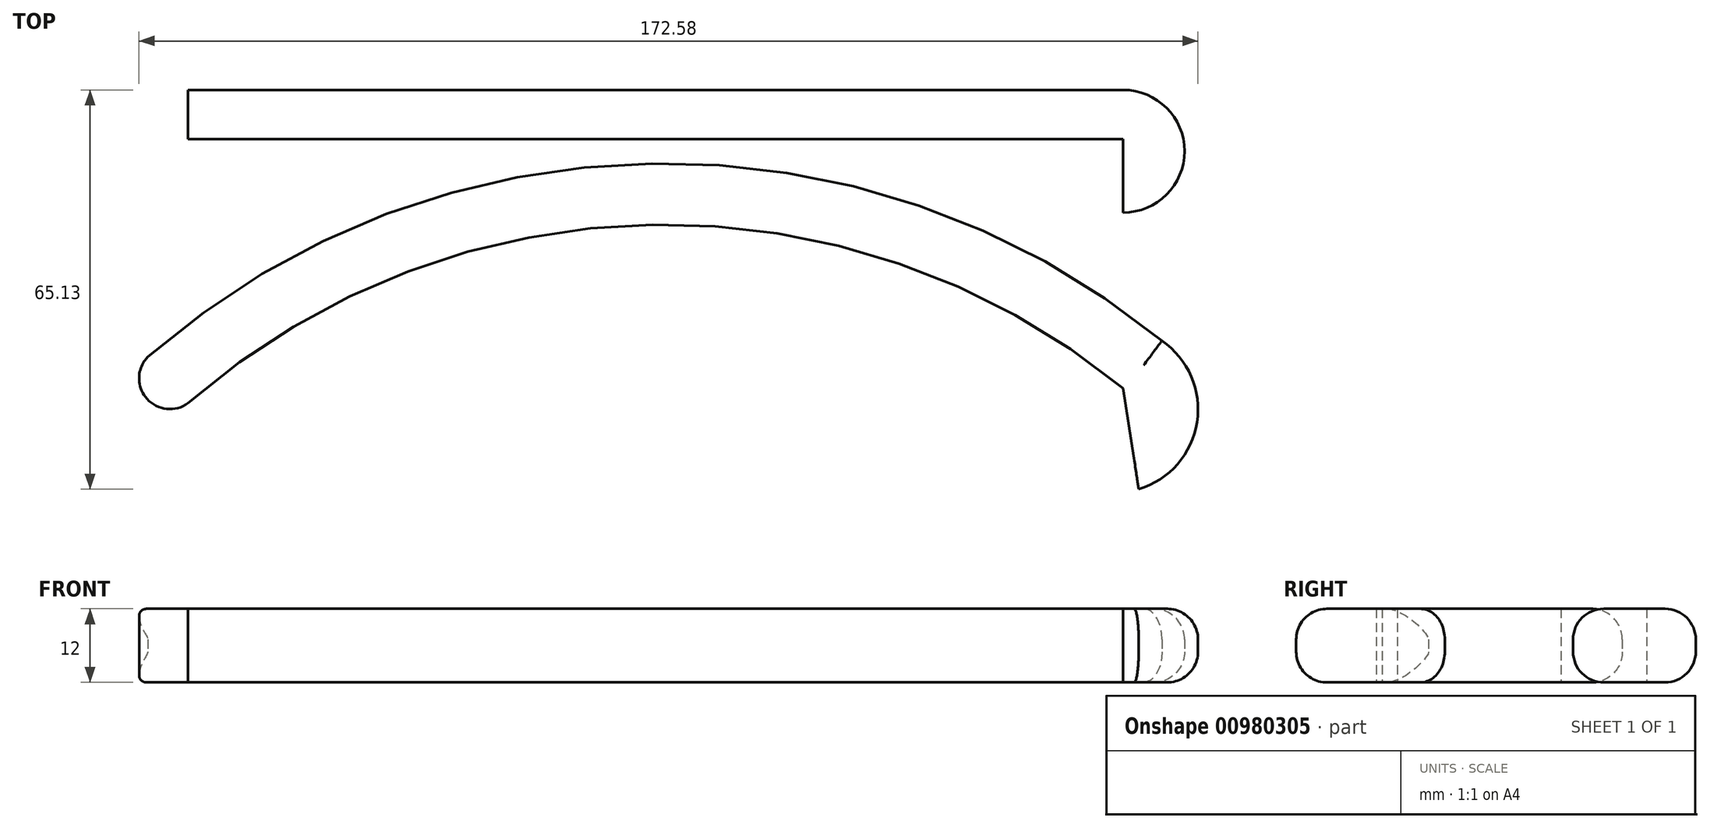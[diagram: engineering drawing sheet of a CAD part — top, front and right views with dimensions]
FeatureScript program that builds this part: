
annotation { "Feature Type Name" : "Feature", "Feature Type Description" : "" }
export const myFeature = defineFeature(function(context is Context, id is Id, definition is map)
    precondition{}
    {
        {
            var Q0;
            Q0=qCreatedBy(makeId("Top.planeOp"),FACE);
            var sketch = newSketch(context, id + "F0", { "sketchPlane" : qUnion([Q0])});
            skLineSegment(sketch, "E0.bottom", {"start": v(-72.52, 25.45) * mm, "end": v(79.88, 25.45) * mm});
            skLineSegment(sketch, "E0.top", {"start": v(-72.52, 17.45) * mm, "end": v(79.88, 17.45) * mm});
            skLineSegment(sketch, "E0.left", {"start": v(-72.52, 25.45) * mm, "end": v(-72.52, 17.45) * mm});
            skLineSegment(sketch, "E0.right", {"start": v(79.88, 25.45) * mm, "end": v(79.88, 17.45) * mm});
            skLineSegment(sketch, "E1", {"start": v(79.88, 17.45) * mm, "end": v(79.88, 5.45) * mm});
            skArc(sketch, "E2", {"start": v(79.88, 5.45) * mm, "mid": v(89.88, 15.45) * mm, "end": v(79.88, 25.45) * mm});
            skArc(sketch, "E3", {"start": v(79.88, -23.2) * mm, "mid": v(3.24, 3.46) * mm, "end": v(-72.52, -25.63) * mm});
            skArc(sketch, "E4.0", {"start": v(86.21, -15.45) * mm, "mid": v(3.08, 13.46) * mm, "end": v(-79.09, -18.1) * mm});
            skArc(sketch, "E5", {"start": v(-79.09, -18.1) * mm, "mid": v(-79.26, -24.88) * mm, "end": v(-72.52, -25.63) * mm});
            skArc(sketch, "E6", {"start": v(82.42, -39.68) * mm, "mid": v(91.92, -28.76) * mm, "end": v(86.21, -15.45) * mm});
            skLineSegment(sketch, "E7", {"start": v(79.88, -23.2) * mm, "end": v(82.42, -39.68) * mm});
            skSolve(sketch);
        }
        {
            var Q0;
            Q0=makeQuery(id+"F0.imprint","IMPRINT",FACE,{"disambiguationData":[TD([[makeQuery(id+"F0.imprint","IMPRINT",EDGE,{"derivedFrom":sQuery(id+"F0.wireOp",EDGE,"E3")}),-1.0]])]});
            var Q1;
            Q1=makeQuery(id+"F0.imprint","IMPRINT",FACE,{"disambiguationData":[TD([[makeQuery(id+"F0.imprint","IMPRINT",EDGE,{"derivedFrom":sQuery(id+"F0.wireOp",EDGE,"E0.bottom")}),-1.0]])]});
            var Q2;
            Q2=makeQuery(id+"F0.imprint","IMPRINT",FACE,{"disambiguationData":[TD([[makeQuery(id+"F0.imprint","IMPRINT",EDGE,{"derivedFrom":sQuery(id+"F0.wireOp",EDGE,"E0.right")}),1.0]])]});
            extrude(context, id + "F1", {"entities" : qUnion([Q0, Q1, Q2]), "depth" : 12 * mm, "offsetDistance" : 25 * mm});
        }
        {
            var Q0;
            Q0=makeQuery(id+"F1.opExtrude","CAP_EDGE",EDGE,{"disambiguationData":[OSD([sQuery(id+"F0.wireOp",EDGE,"E0.bottom")])],"isStart":true});
            var Q1;
            Q1=makeQuery(id+"F1.opExtrude","CAP_EDGE",EDGE,{"disambiguationData":[OSD([sQuery(id+"F0.wireOp",EDGE,"E0.bottom")])],"isStart":false});
            fillet(context, id + "F2", {"entities" : qUnion([Q0, Q1]), "radius" : 5 * mm, "tangentPropagation" : true, "allowEdgeOverflow" : false});
        }
        {
            var Q0;
            Q0=makeQuery(id+"F1.opExtrude","CAP_EDGE",EDGE,{"disambiguationData":[OSD([sQuery(id+"F0.wireOp",EDGE,"E4.0")])],"isStart":true});
            var Q1;
            Q1=makeQuery(id+"F1.opExtrude","CAP_EDGE",EDGE,{"disambiguationData":[OSD([sQuery(id+"F0.wireOp",EDGE,"E4.0")])],"isStart":false});
            var Q2;
            Q2=makeQuery(id+"F1.opExtrude","CAP_EDGE",EDGE,{"disambiguationData":[OSD([sQuery(id+"F0.wireOp",EDGE,"E6")])],"isStart":true});
            var Q3;
            Q3=makeQuery(id+"F1.opExtrude","CAP_EDGE",EDGE,{"disambiguationData":[OSD([sQuery(id+"F0.wireOp",EDGE,"E6")])],"isStart":false});
            fillet(context, id + "F3", {"entities" : qUnion([Q0, Q1, Q2, Q3]), "radius" : 5 * mm, "tangentPropagation" : true, "allowEdgeOverflow" : false});
        }
    });
